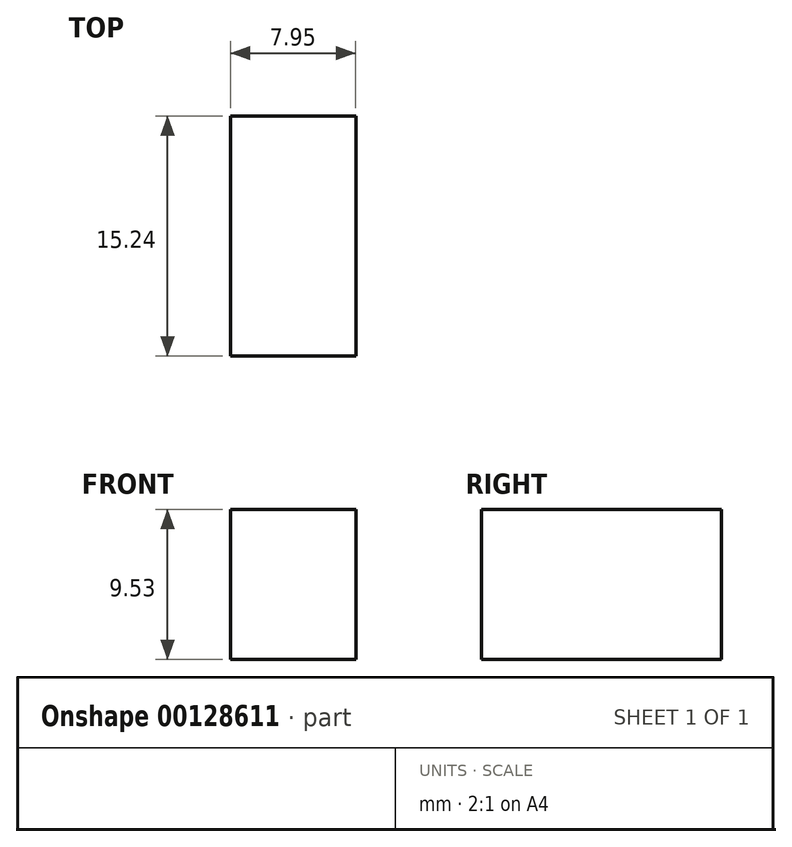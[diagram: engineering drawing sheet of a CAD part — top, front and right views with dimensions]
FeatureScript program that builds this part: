
annotation { "Feature Type Name" : "Feature", "Feature Type Description" : "" }
export const myFeature = defineFeature(function(context is Context, id is Id, definition is map)
    precondition{}
    {
        {
            var Q0;
            Q0=qCreatedBy(makeId("Front.planeOp"),FACE);
            var sketch = newSketch(context, id + "F0", { "sketchPlane" : qUnion([Q0])});
            skLineSegment(sketch, "E0.bottom", {"start": v(-36.7, 16.49) * mm, "end": v(-28.76, 16.49) * mm});
            skLineSegment(sketch, "E0.top", {"start": v(-36.7, 6.96) * mm, "end": v(-28.76, 6.96) * mm});
            skLineSegment(sketch, "E0.left", {"start": v(-36.7, 16.49) * mm, "end": v(-36.7, 6.96) * mm});
            skLineSegment(sketch, "E0.right", {"start": v(-28.76, 16.49) * mm, "end": v(-28.76, 6.96) * mm});
            skSolve(sketch);
        }
        {
            var Q0;
            Q0=makeQuery(id+"F0.imprint","IMPRINT",FACE,{"disambiguationData":[TD([[makeQuery(id+"F0.imprint","IMPRINT",EDGE,{"derivedFrom":sQuery(id+"F0.wireOp",EDGE,"E0.bottom")}),-1.0]])]});
            extrude(context, id + "F1", {"entities" : qUnion([Q0]), "depth" : 15.24 * mm});
        }
    });
